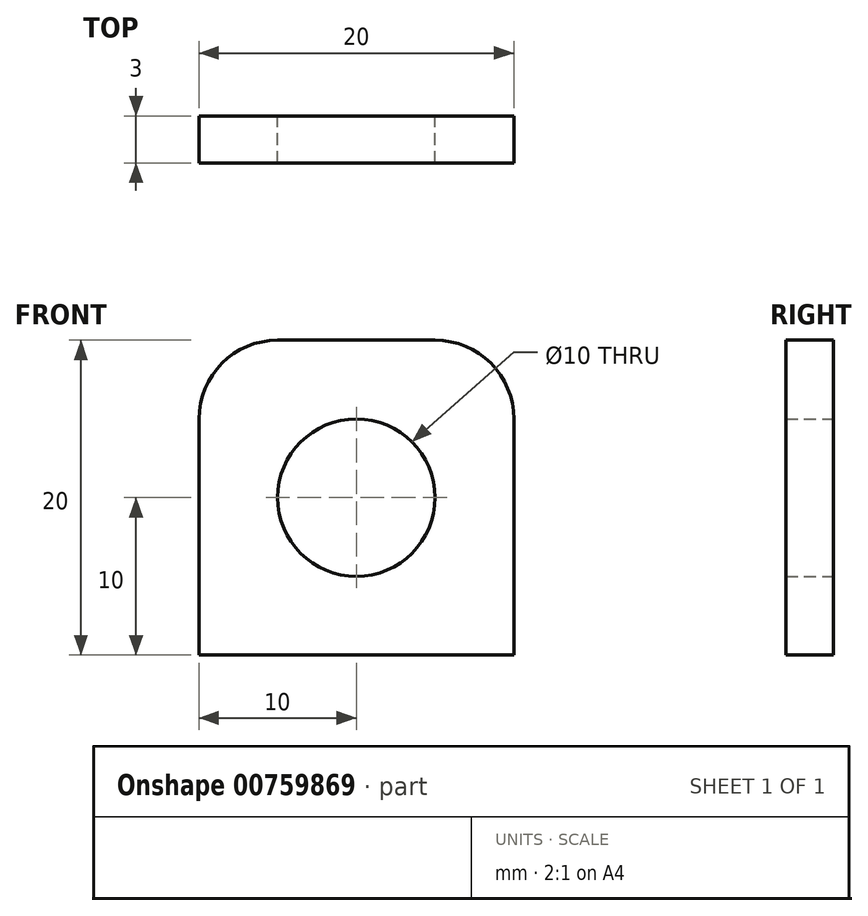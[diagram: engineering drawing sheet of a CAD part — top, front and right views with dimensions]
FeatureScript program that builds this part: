
annotation { "Feature Type Name" : "Feature", "Feature Type Description" : "" }
export const myFeature = defineFeature(function(context is Context, id is Id, definition is map)
    precondition{}
    {
        {
            var Q0;
            Q0=qCreatedBy(makeId("Front.planeOp"),FACE);
            var sketch = newSketch(context, id + "F0", { "sketchPlane" : qUnion([Q0])});
            skLineSegment(sketch, "E0.bottom", {"start": v(10, 10) * mm, "end": v(-10, 10) * mm});
            skLineSegment(sketch, "E0.top", {"start": v(10, -10) * mm, "end": v(-10, -10) * mm});
            skLineSegment(sketch, "E0.left", {"start": v(10, 10) * mm, "end": v(10, -10) * mm});
            skLineSegment(sketch, "E0.right", {"start": v(-10, 10) * mm, "end": v(-10, -10) * mm});
            skPoint(sketch, "E0.middle", {"position": v(0, 0) * mm});
            skCircle(sketch, "E1", {"center": v(0, 0) * mm, "radius": 5 * mm});
            skSolve(sketch);
        }
        {
            var Q0;
            Q0=makeQuery(id+"F0.imprint","IMPRINT",FACE,{"disambiguationData":[TD([[makeQuery(id+"F0.imprint","IMPRINT",EDGE,{"derivedFrom":sQuery(id+"F0.wireOp",EDGE,"E0.bottom")}),1.0]])]});
            extrude(context, id + "F1", {"entities" : qUnion([Q0]), "depth" : 3 * mm, "offsetDistance" : 25 * mm});
        }
        {
            var Q0;
            Q0=makeQuery(id+"F1.opExtrude","SWEPT_EDGE",EDGE,{"disambiguationData":[OSD([sQuery(id+"F0.wireOp",EDGE,"E0.bottom"),sQuery(id+"F0.wireOp",EDGE,"E0.left")])]});
            var Q1;
            Q1=makeQuery(id+"F1.opExtrude","SWEPT_EDGE",EDGE,{"disambiguationData":[OSD([sQuery(id+"F0.wireOp",EDGE,"E0.bottom"),sQuery(id+"F0.wireOp",EDGE,"E0.right")])]});
            fillet(context, id + "F2", {"entities" : qUnion([Q0, Q1]), "radius" : 5 * mm, "tangentPropagation" : true, "allowEdgeOverflow" : false});
        }
    });
